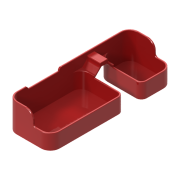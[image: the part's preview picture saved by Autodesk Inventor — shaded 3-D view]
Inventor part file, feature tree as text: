
AUTODESK INVENTOR PART (.ipt)
format: ipt  version: 2021 (Build 250183000, 183)  size: 286,208 bytes
history: native  units: mm
features: extrude x1, fillet x1, chamfer x1, sketch x1
ambient origin geometry x8: Origin, YZ Plane, XZ Plane, XY Plane, X Axis, Y Axis, Z Axis, Center Point
bodies: Volumenkörper1 (feature_tree), Body1 (feature_tree)
feature tree (4):
  extrude  "Extrusion1"  Depth=3.5mm
  fillet  "Rundung1"  Radius=38.0mm
  chamfer  "Fase1"  Distance=10.0mm
  sketch  "Skizze1"  dims[d0=89.0mm d1=3.5mm d2=38.0mm d3=10.0mm d4=0.0mm d5=3.5mm d6=0.4mm d7=2.0mm d8=45.0deg]
